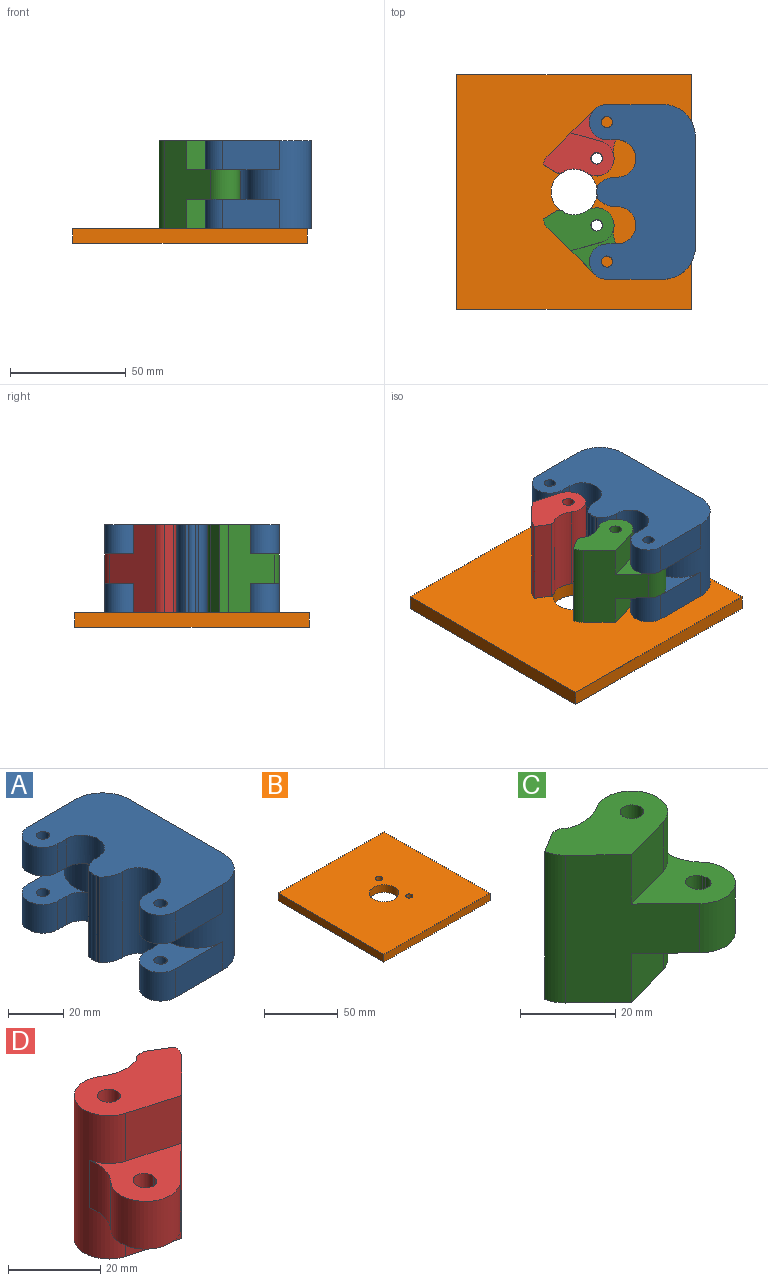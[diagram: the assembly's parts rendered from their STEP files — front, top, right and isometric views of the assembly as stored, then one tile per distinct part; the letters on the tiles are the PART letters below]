
ASSEMBLY  parts=4 mates=3
PART A: 41 faces, bbox 45.9x75.6x38.1 mm
  f0: plane 47.75x38.1mm, normal (1,0,0), area 1454.6mm2, adj f1,f2,f10,f11,f32,f37,f39
  f1: cylinder r=13.92mm len=38.1mm, axis (0,0,-1), area 1188.4mm2, adj f0,f8,f10,f11,f18,f21,f28,f31
  f2: cylinder r=13.92mm len=38.1mm, axis (0,0,-1), area 1188.4mm2, adj f0,f7,f10,f11,f13,f16,f23,f26
  f3: plane 38.1x1.38mm, normal (-1,0,0), area 52.4mm2, adj f4,f9,f10,f11
  f4: cylinder r=2.41mm len=38.1mm, axis (0,0,-1), area 121.5mm2, adj f3,f5,f10,f11
  f5: plane 38.1x1.38mm, normal (-1,0,0), area 52.4mm2, adj f4,f6,f10,f11
  f6: cylinder r=10.61mm len=38.1mm, axis (0,0,-1), area 352.2mm2, adj f5,f7,f10,f11
  f7: cylinder r=8.09mm len=38.1mm, axis (0,0,-1), area 862mm2, adj f2,f6,f10,f11,f15,f16,f25,f26
  f8: cylinder r=8.09mm len=38.1mm, axis (0,0,-1), area 862mm2, adj f1,f9,f10,f11,f17,f21,f27,f31
  f9: cylinder r=10.61mm len=38.1mm, axis (0,0,-1), area 352.2mm2, adj f3,f8,f10,f11
  f10: plane 75.59x45.87mm, normal (0,0,1), area 2639.8mm2, adj f0,f1,f2,f3,f4,f5,f6,f7
  f11: plane 75.59x45.87mm, normal (0,0,-1), area 2639.8mm2, adj f0,f1,f2,f3,f4,f5,f6,f7
  f12: cylinder r=7.61mm len=15.22mm, axis (0,0,-1), area 303.7mm2, adj f11,f13,f15,f16
  f13: plane 24.34x12.7mm, normal (0,-1,0), area 309.1mm2, adj f2,f11,f12,f16
  f14: cylinder r=2.41mm len=12.7mm, axis (0,0,-1), area 192.5mm2, adj f11,f16
  f15: plane 12.7x4.44mm, normal (0,1,0), area 56.4mm2, adj f7,f11,f12,f16
  f16: plane 31.95x19.86mm, normal (0,0,1), area 279mm2, adj f2,f7,f12,f13,f14,f15
  f17: plane 12.7x4.44mm, normal (0,-1,0), area 56.4mm2, adj f8,f11,f20,f21
  f18: plane 24.34x12.7mm, normal (0,1,0), area 309.1mm2, adj f1,f11,f20,f21
  f19: cylinder r=2.41mm len=12.7mm, axis (0,0,-1), area 192.5mm2, adj f11,f21
  f20: cylinder r=7.61mm len=15.22mm, axis (0,0,-1), area 303.7mm2, adj f11,f17,f18,f21
  f21: plane 31.95x19.86mm, normal (0,0,1), area 279mm2, adj f1,f8,f17,f18,f19,f20
  f22: cylinder r=7.61mm len=15.22mm, axis (0,0,-1), area 303.7mm2, adj f10,f23,f25,f26
  f23: plane 24.34x12.7mm, normal (0,-1,0), area 309.1mm2, adj f2,f10,f22,f26
  f24: cylinder r=2.41mm len=12.7mm, axis (0,0,-1), area 192.5mm2, adj f10,f26
  f25: plane 12.7x4.44mm, normal (0,1,0), area 56.4mm2, adj f7,f10,f22,f26
  f26: plane 31.95x19.86mm, normal (0,0,-1), area 279mm2, adj f2,f7,f22,f23,f24,f25
  f27: plane 12.7x4.44mm, normal (0,-1,0), area 56.4mm2, adj f8,f10,f30,f31
  f28: plane 24.34x12.7mm, normal (0,1,0), area 309.1mm2, adj f1,f10,f30,f31
  f29: cylinder r=2.41mm len=12.7mm, axis (0,0,-1), area 192.5mm2, adj f10,f31
  f30: cylinder r=7.61mm len=15.22mm, axis (0,0,-1), area 303.7mm2, adj f10,f27,f28,f31
  f31: plane 31.95x19.86mm, normal (0,0,-1), area 279mm2, adj f1,f8,f27,f28,f29,f30
  f32: cone r=10.16mm half-angle=60deg, axis (1,0,0), area 81.8mm2, adj f0,f33
  f33: cone r=9.65mm half-angle=60deg, axis (-1,0,0), area 32.5mm2, adj f32,f34
  f34: cylinder r=9.78mm len=19.55mm, axis (1,0,0), area 324.7mm2, adj f33,f36
  f35: plane 14.78x14.78mm, normal (1,0,0), area 171.7mm2, adj f36
  f36: cone r=7.45mm half-angle=60deg, axis (1,0,0), area 126.9mm2, adj f34,f35
  f37: cylinder r=2.54mm len=19.05mm, axis (1,0,0), area 304mm2, adj f0,f38
  f38: plane 5.08x5.08mm, normal (1,0,0), area 20.3mm2, adj f37
  f39: cylinder r=2.54mm len=19.05mm, axis (1,0,0), area 304mm2, adj f0,f40
  f40: plane 5.08x5.08mm, normal (1,0,0), area 20.3mm2, adj f39
PART B: 9 faces, bbox 101.6x101.6x6.4 mm
  f0: plane 101.6x6.35mm, normal (0,-1,0), area 645.2mm2, adj f1,f6,f7,f8
  f1: plane 101.6x6.35mm, normal (1,0,0), area 645.2mm2, adj f0,f2,f7,f8
  f2: plane 101.6x6.35mm, normal (0,1,0), area 645.2mm2, adj f1,f6,f7,f8
  f3: cylinder r=2.41mm len=6.35mm, axis (0,0,-1), area 96.3mm2, adj f7,f8
  f4: cylinder r=2.41mm len=6.35mm, axis (0,0,-1), area 96.3mm2, adj f7,f8
  f5: cylinder r=9.97mm len=19.95mm, axis (0,0,-1), area 398mm2, adj f7,f8
  f6: plane 101.6x6.35mm, normal (-1,0,0), area 645.2mm2, adj f0,f2,f7,f8
  f7: plane 101.6x101.6mm, normal (0,0,1), area 9973.4mm2, adj f0,f1,f2,f3,f4,f5,f6
  f8: plane 101.6x101.6mm, normal (0,0,-1), area 9973.4mm2, adj f0,f1,f2,f3,f4,f5,f6
PART C: 20 faces, bbox 35.2x30.8x38.1 mm
  f0: plane 13.23x12.7mm, normal (0.27,-0.96,0), area 174.6mm2, adj f6,f8,f11,f19
  f1: cylinder r=10.61mm len=38.1mm, axis (0,0,-1), area 382.2mm2, adj f2,f8,f10,f11
  f2: cylinder r=2.41mm len=38.1mm, axis (0,0,-1), area 121.5mm2, adj f1,f3,f10,f11
  f3: plane 38.1x0.52mm, normal (0.36,0.93,0), area 21.2mm2, adj f2,f4,f10,f11
  f4: plane 38.1x6.16mm, normal (-0.52,0.85,0), area 275.1mm2, adj f3,f5,f10,f11
  f5: cylinder r=7.49mm len=38.1mm, axis (0,0,-1), area 178.9mm2, adj f4,f6,f10,f11
  f6: plane 38.1x20.21mm, normal (-0.7,-0.72,0), area 710.2mm2, adj f0,f5,f7,f10,f11,f15,f18,f19
  f7: plane 13.23x12.7mm, normal (0.27,-0.96,0), area 174.6mm2, adj f6,f8,f10,f18
  f8: cylinder r=7.56mm len=38.1mm, axis (0,0,-1), area 887.2mm2, adj f0,f1,f7,f10,f11,f16,f18,f19
  f9: cylinder r=2.48mm len=38.1mm, axis (0,0,-1), area 594mm2, adj f10,f11
  f10: plane 30.77x18.58mm, normal (0,0,1), area 363.5mm2, adj f1,f2,f3,f4,f5,f6,f7,f8
  f11: plane 30.77x18.58mm, normal (0,0,-1), area 363.5mm2, adj f0,f1,f2,f3,f4,f5,f6,f8
  f12: cylinder r=2.43mm len=12.7mm, axis (0,0,-1), area 97mm2, adj f13,f17,f18,f19
  f13: plane 12.7x0.59mm, normal (0.96,0.27,0), area 7.8mm2, adj f12,f14,f18,f19
  f14: cylinder r=2.43mm len=12.7mm, axis (0,0,-1), area 97mm2, adj f13,f17,f18,f19
  f15: cylinder r=7.56mm len=12.85mm, axis (0,0,-1), area 296.4mm2, adj f6,f16,f18,f19
  f16: cylinder r=10.61mm len=12.7mm, axis (0,0,-1), area 125.5mm2, adj f8,f15,f18,f19
  f17: plane 12.7x0.59mm, normal (-0.96,-0.27,0), area 7.8mm2, adj f12,f14,f18,f19
  f18: plane 23.17x21.84mm, normal (0,0,1), area 229.9mm2, adj f6,f7,f8,f12,f13,f14,f15,f16
  f19: plane 23.17x21.84mm, normal (0,0,-1), area 229.9mm2, adj f0,f6,f8,f12,f13,f14,f15,f16
PART D: 20 faces, bbox 35.2x30.8x38.1 mm
  f0: plane 13.23x12.7mm, normal (-0.27,-0.96,0), area 174.6mm2, adj f4,f6,f11,f19
  f1: plane 38.1x0.52mm, normal (-0.36,0.93,0), area 21.2mm2, adj f2,f8,f10,f11
  f2: cylinder r=2.41mm len=38.1mm, axis (0,0,-1), area 121.5mm2, adj f1,f3,f10,f11
  f3: cylinder r=10.61mm len=38.1mm, axis (0,0,-1), area 382.2mm2, adj f2,f4,f10,f11
  f4: cylinder r=7.56mm len=38.1mm, axis (0,0,-1), area 887.2mm2, adj f0,f3,f5,f10,f11,f12,f18,f19
  f5: plane 13.23x12.7mm, normal (-0.27,-0.96,0), area 174.6mm2, adj f4,f6,f10,f18
  f6: plane 38.1x20.21mm, normal (0.7,-0.72,0), area 710.2mm2, adj f0,f5,f7,f10,f11,f13,f18,f19
  f7: cylinder r=7.49mm len=38.1mm, axis (0,0,-1), area 178.9mm2, adj f6,f8,f10,f11
  f8: plane 38.1x6.16mm, normal (0.52,0.85,0), area 275.1mm2, adj f1,f7,f10,f11
  f9: cylinder r=2.48mm len=38.1mm, axis (0,0,-1), area 594mm2, adj f10,f11
  f10: plane 30.77x18.58mm, normal (0,0,1), area 363.5mm2, adj f1,f2,f3,f4,f5,f6,f7,f8
  f11: plane 30.77x18.58mm, normal (0,0,-1), area 363.5mm2, adj f0,f1,f2,f3,f4,f6,f7,f8
  f12: cylinder r=10.61mm len=12.7mm, axis (0,0,-1), area 125.5mm2, adj f4,f13,f18,f19
  f13: cylinder r=7.56mm len=12.85mm, axis (0,0,-1), area 296.4mm2, adj f6,f12,f18,f19
  f14: cylinder r=2.43mm len=12.7mm, axis (0,0,-1), area 97mm2, adj f15,f17,f18,f19
  f15: plane 12.7x0.59mm, normal (-0.96,0.27,0), area 7.8mm2, adj f14,f16,f18,f19
  f16: cylinder r=2.43mm len=12.7mm, axis (0,0,-1), area 97mm2, adj f15,f17,f18,f19
  f17: plane 12.7x0.59mm, normal (0.96,-0.27,0), area 7.8mm2, adj f14,f16,f18,f19
  f18: plane 23.17x21.84mm, normal (0,0,1), area 229.9mm2, adj f4,f5,f6,f12,f13,f14,f15,f16
  f19: plane 23.17x21.84mm, normal (0,0,-1), area 229.9mm2, adj f0,f4,f6,f12,f13,f14,f15,f16
PLACE A t=(-53.84,0,6.35)mm
PLACE B at identity fixed
PLACE C t=(0,63.5,6.35)mm
PLACE D rot(axis=(0,0,1),180deg) t=(-32.05,-63.5,6.35)mm
MATE revolute D.f4 <-> B.f3  axis (0,0,-1) through (9.78,14.48,6.35)mm
MATE revolute C.f8 <-> B.f4  axis (0,0,-1) through (9.78,-14.48,6.35)mm
MATE slider A.f0 <-> B.f1  axis (1,0,0) through (52.45,0,6.35)mm
